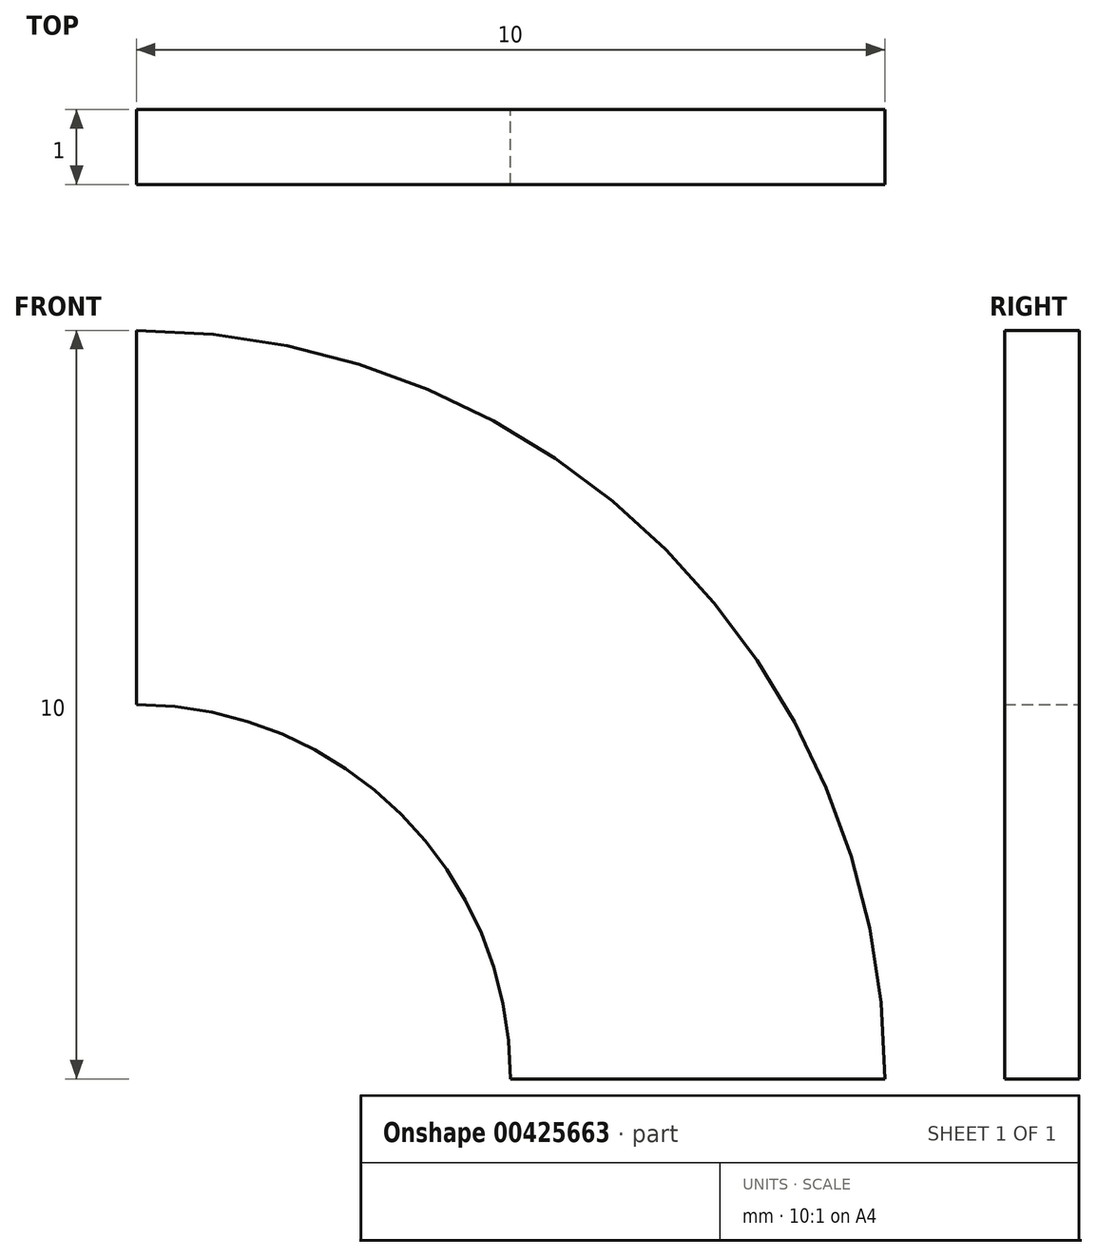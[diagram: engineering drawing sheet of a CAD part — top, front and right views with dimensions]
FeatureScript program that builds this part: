
annotation { "Feature Type Name" : "Feature", "Feature Type Description" : "" }
export const myFeature = defineFeature(function(context is Context, id is Id, definition is map)
    precondition{}
    {
        {
            var Q0;
            Q0=qCreatedBy(makeId("Front.planeOp"),FACE);
            var sketch = newSketch(context, id + "F0", { "sketchPlane" : qUnion([Q0])});
            skLineSegment(sketch, "E0", {"start": v(0, 5) * mm, "end": v(0, 10) * mm});
            skLineSegment(sketch, "E1", {"start": v(5, 0) * mm, "end": v(10, 0) * mm});
            skArc(sketch, "E2", {"start": v(5, 0) * mm, "mid": v(3.54, 3.54) * mm, "end": v(0, 5) * mm});
            skArc(sketch, "E3", {"start": v(10, 0) * mm, "mid": v(7.07, 7.07) * mm, "end": v(0, 10) * mm});
            skSolve(sketch);
        }
        {
            var Q0;
            Q0=makeQuery(id+"F0.imprint","IMPRINT",FACE,{"disambiguationData":[TD([[makeQuery(id+"F0.imprint","IMPRINT",EDGE,{"derivedFrom":sQuery(id+"F0.wireOp",EDGE,"E0")}),-1.0]])]});
            extrude(context, id + "F1", {"entities" : qUnion([Q0]), "depth" : 1 * mm});
        }
    });
